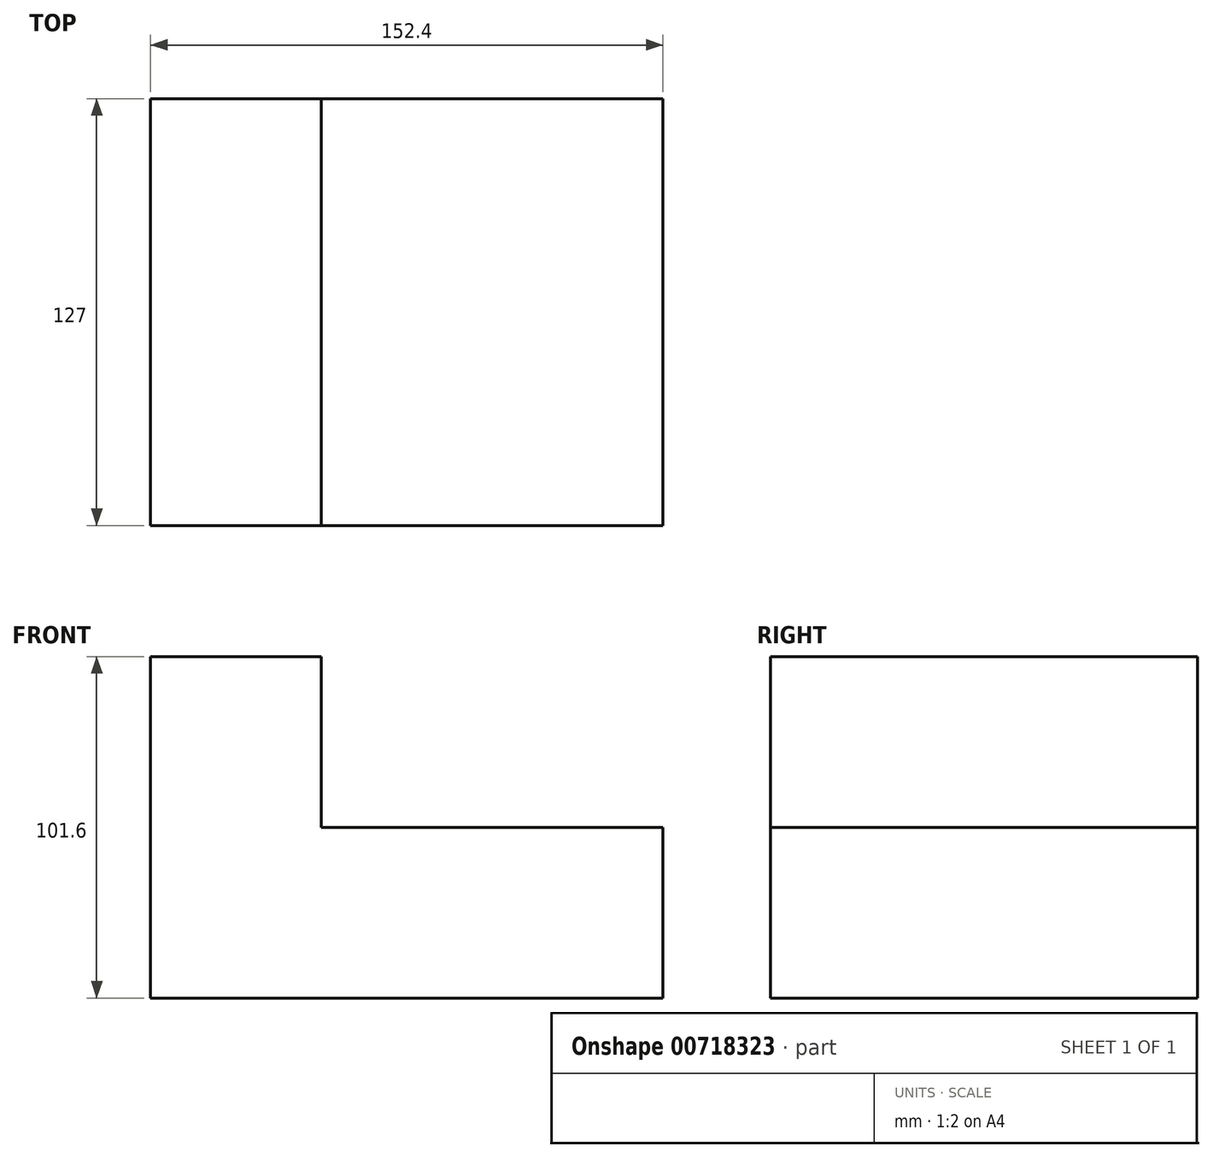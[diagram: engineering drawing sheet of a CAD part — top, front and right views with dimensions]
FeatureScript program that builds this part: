
annotation { "Feature Type Name" : "Feature", "Feature Type Description" : "" }
export const myFeature = defineFeature(function(context is Context, id is Id, definition is map)
    precondition{}
    {
        {
            var Q0;
            Q0=qCreatedBy(makeId("Front.planeOp"),FACE);
            var sketch = newSketch(context, id + "F0", { "sketchPlane" : qUnion([Q0])});
            skLineSegment(sketch, "E0", {"start": v(-99.43, -59.72) * mm, "end": v(52.97, -59.72) * mm});
            skLineSegment(sketch, "E1", {"start": v(52.97, -59.72) * mm, "end": v(52.97, -8.92) * mm});
            skLineSegment(sketch, "E2", {"start": v(52.97, -8.92) * mm, "end": v(-48.63, -8.92) * mm});
            skLineSegment(sketch, "E3", {"start": v(-48.63, -8.92) * mm, "end": v(-48.63, 41.88) * mm});
            skLineSegment(sketch, "E4", {"start": v(-48.63, 41.88) * mm, "end": v(-99.43, 41.88) * mm});
            skLineSegment(sketch, "E5", {"start": v(-99.43, 41.88) * mm, "end": v(-99.43, -59.72) * mm});
            skSolve(sketch);
        }
        {
            var Q0;
            Q0=makeQuery(id+"F0.imprint","IMPRINT",FACE,{"disambiguationData":[TD([[makeQuery(id+"F0.imprint","IMPRINT",EDGE,{"derivedFrom":sQuery(id+"F0.wireOp",EDGE,"E0")}),1.0]])]});
            extrude(context, id + "F1", {"entities" : qUnion([Q0]), "depth" : 127 * mm, "offsetDistance" : 25.4 * mm});
        }
    });
